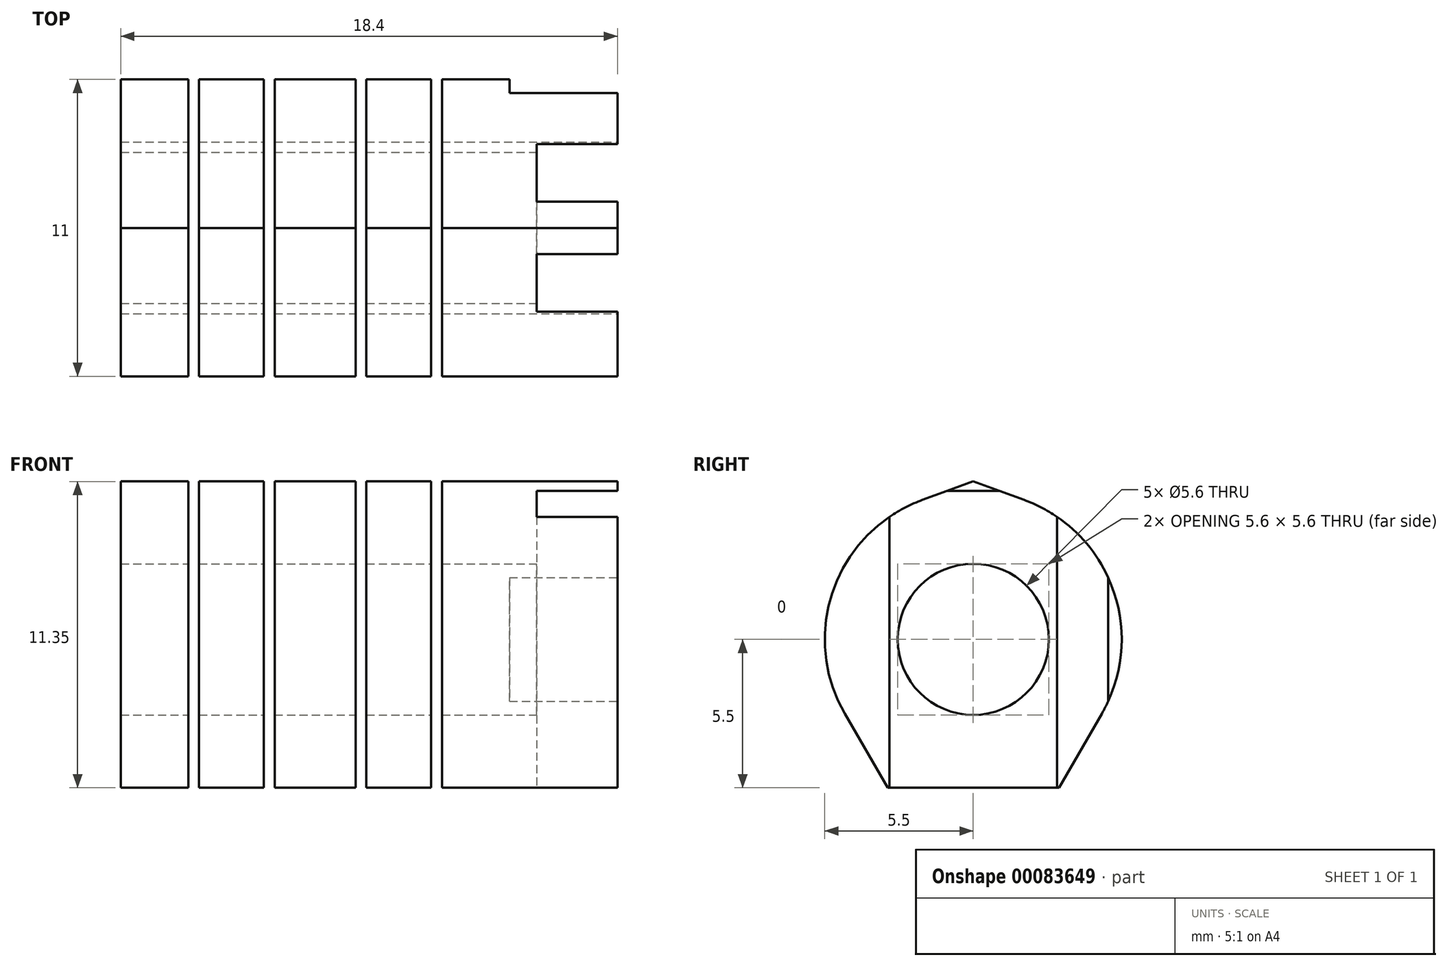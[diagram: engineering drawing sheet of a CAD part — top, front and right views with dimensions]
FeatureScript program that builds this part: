
annotation { "Feature Type Name" : "Feature", "Feature Type Description" : "" }
export const myFeature = defineFeature(function(context is Context, id is Id, definition is map)
    precondition{}
    {
        {
            var Q0;
            Q0=qCreatedBy(makeId("Top.planeOp"),FACE);
            var sketch = newSketch(context, id + "F0", { "sketchPlane" : qUnion([Q0])});
            skLineSegment(sketch, "E0", {"start": v(0, 0) * mm, "end": v(0, 9.5) * mm, "construction": true});
            skLineSegment(sketch, "E1", {"start": v(0, 5.5) * mm, "end": v(1.5, 5.5) * mm});
            skLineSegment(sketch, "E2", {"start": v(1.5, 5.5) * mm, "end": v(1.5, -8) * mm});
            skLineSegment(sketch, "E3", {"start": v(1.5, -8) * mm, "end": v(4.7, -8) * mm});
            skLineSegment(sketch, "E4", {"start": v(4.7, -8) * mm, "end": v(4.7, 5.5) * mm});
            skLineSegment(sketch, "E5", {"start": v(4.7, 5.5) * mm, "end": v(7.2, 5.5) * mm});
            skLineSegment(sketch, "E6", {"start": v(7.2, 5.5) * mm, "end": v(7.2, 5) * mm});
            skLineSegment(sketch, "E7", {"start": v(7.2, 5) * mm, "end": v(11.2, 5) * mm});
            skLineSegment(sketch, "E8", {"start": v(11.2, 5) * mm, "end": v(11.2, -9) * mm});
            skLineSegment(sketch, "E9", {"start": v(11.2, -9) * mm, "end": v(-7.2, -9) * mm});
            skLineSegment(sketch, "E10", {"start": v(-7.2, -9) * mm, "end": v(-7.2, 5.5) * mm});
            skLineSegment(sketch, "E11", {"start": v(-7.2, 5.5) * mm, "end": v(-4.7, 5.5) * mm});
            skLineSegment(sketch, "E12", {"start": v(-4.7, 5.5) * mm, "end": v(-4.7, -8) * mm});
            skLineSegment(sketch, "E13", {"start": v(-4.7, -8) * mm, "end": v(-1.5, -8) * mm});
            skLineSegment(sketch, "E14", {"start": v(-1.5, -8) * mm, "end": v(-1.5, 5.5) * mm});
            skLineSegment(sketch, "E15", {"start": v(-1.5, 5.5) * mm, "end": v(0, 5.5) * mm});
            skLineSegment(sketch, "E16", {"start": v(-4.7, 5.5) * mm, "end": v(-1.5, 5.5) * mm, "construction": true});
            skLineSegment(sketch, "E17", {"start": v(1.5, 5.5) * mm, "end": v(4.7, 5.5) * mm, "construction": true});
            skLineSegment(sketch, "E18", {"start": v(0, 9.5) * mm, "end": v(-7.3, 9.5) * mm});
            skLineSegment(sketch, "E19", {"start": v(-7.3, 9.5) * mm, "end": v(-7.3, 8.5) * mm});
            skLineSegment(sketch, "E20", {"start": v(-7.3, 8.5) * mm, "end": v(-4.3, 8.5) * mm});
            skLineSegment(sketch, "E21", {"start": v(-4.3, 8.5) * mm, "end": v(-4.3, -6.5) * mm});
            skLineSegment(sketch, "E22", {"start": v(-4.3, -6.5) * mm, "end": v(-1.9, -6.5) * mm});
            skLineSegment(sketch, "E23", {"start": v(-1.9, -6.5) * mm, "end": v(-1.9, 8.5) * mm});
            skPoint(sketch, "E23.endSnap0", {"position": v(-5.8, 8.5) * mm});
            skLineSegment(sketch, "E24", {"start": v(-1.9, 8.5) * mm, "end": v(0, 8.5) * mm});
            skLineSegment(sketch, "E25.MirrorCS", {"start": v(0, 9.5) * mm, "end": v(7.3, 9.5) * mm});
            skLineSegment(sketch, "E26.MirrorCS", {"start": v(7.3, 9.5) * mm, "end": v(7.3, 8.5) * mm});
            skLineSegment(sketch, "E27.MirrorCS", {"start": v(7.3, 8.5) * mm, "end": v(4.3, 8.5) * mm});
            skLineSegment(sketch, "E28.MirrorCS", {"start": v(4.3, 8.5) * mm, "end": v(4.3, -6.5) * mm});
            skLineSegment(sketch, "E29.MirrorCS", {"start": v(1.9, -6.5) * mm, "end": v(1.9, 8.5) * mm});
            skLineSegment(sketch, "E30.MirrorCS", {"start": v(1.9, 8.5) * mm, "end": v(0, 8.5) * mm});
            skLineSegment(sketch, "E31.MirrorCS", {"start": v(4.3, -6.5) * mm, "end": v(1.9, -6.5) * mm});
            skLineSegment(sketch, "E32", {"start": v(0, 0) * mm, "end": v(0, -9) * mm, "construction": true});
            skLineSegment(sketch, "E33", {"start": v(1.9, 8.5) * mm, "end": v(4.3, 8.5) * mm, "construction": true});
            skPoint(sketch, "E34", {"position": v(3.1, 8.5) * mm});
            skPoint(sketch, "E35", {"position": v(3.1, -8) * mm});
            skSolve(sketch);
        }
        {
            var Q0;
            Q0=makeQuery(id+"F0.imprint","IMPRINT",FACE,{"disambiguationData":[TD([[makeQuery(id+"F0.imprint","IMPRINT",EDGE,{"derivedFrom":sQuery(id+"F0.wireOp",EDGE,"E18")}),1.0]])]});
            var Q1;
            Q1=makeQuery(id+"F0.imprint","IMPRINT",FACE,{"disambiguationData":[TD([[makeQuery(id+"F0.imprint","IMPRINT",EDGE,{"derivedFrom":sQuery(id+"F0.wireOp",EDGE,"E1")}),-1.0]])]});
            extrude(context, id + "F1", {"entities" : qUnion([Q0, Q1]), "depth" : 25 * mm});
        }
        {
            var Q0;
            Q0=qCreatedBy(makeId("Right.planeOp"),FACE);
            var sketch = newSketch(context, id + "F2", { "sketchPlane" : qUnion([Q0])});
            skLineSegment(sketch, "E36", {"start": v(0, 0) * mm, "end": v(0, 5.5) * mm, "construction": true});
            skCircle(sketch, "E37", {"center": v(0, 5.5) * mm, "radius": 2.8 * mm});
            skCircle(sketch, "E38", {"center": v(0, 5.5) * mm, "radius": 5.5 * mm});
            skLineSegment(sketch, "E39", {"start": v(1.88, 10.67) * mm, "end": v(-37.5, 25) * mm});
            skLineSegment(sketch, "E40", {"start": v(-1.88, 10.67) * mm, "end": v(37.5, 25) * mm});
            skLineSegment(sketch, "E41", {"start": v(-37.5, 25) * mm, "end": v(37.5, 25) * mm});
            skLineSegment(sketch, "E42", {"start": v(-37.5, 25) * mm, "end": v(-37.5, 0) * mm});
            skLineSegment(sketch, "E43", {"start": v(-37.5, 0) * mm, "end": v(0, 0) * mm});
            skLineSegment(sketch, "E44", {"start": v(0, 0) * mm, "end": v(37.5, 0) * mm});
            skLineSegment(sketch, "E45", {"start": v(37.5, 0) * mm, "end": v(37.5, 25) * mm});
            skLineSegment(sketch, "E46", {"start": v(-4.76, 2.75) * mm, "end": v(-3.18, 0) * mm});
            skLineSegment(sketch, "E47", {"start": v(4.76, 2.75) * mm, "end": v(3.18, 0) * mm});
            skSolve(sketch);
        }
        {
            var Q0;
            Q0=makeQuery(id+"F2.imprint","IMPRINT",FACE,{"disambiguationData":[TD([[makeQuery(id+"F2.imprint","IMPRINT",EDGE,{"derivedFrom":sQuery(id+"F2.wireOp",EDGE,"E37")}),1.0]])]});
            extrude(context, id + "F3", {"entities" : qUnion([Q0]), "operationType" : NewBodyOperationType.REMOVE, "endBound" : BoundingType.THROUGH_ALL, "oppositeDirection" : true, "depth" : 25 * mm, "hasSecondDirection" : true, "secondDirectionBound" : SecondDirectionBoundingType.THROUGH_ALL, "secondDirectionOppositeDirection" : false, "secondDirectionDepth" : 25 * mm});
        }
        {
            var Q0;
            {var subQ0=sQuery(id+"F2.wireOp",EDGE,"E41");Q0=makeQuery(id+"F2.imprint","IMPRINT",FACE,{"disambiguationData":[TD([[makeQuery(id+"F2.imprint","IMPRINT",EDGE,{"derivedFrom":subQ0}),-1.0]])]});}
            var Q1;
            {var subQ0=sQuery(id+"F2.wireOp",EDGE,"E45");Q1=makeQuery(id+"F2.imprint","IMPRINT",FACE,{"disambiguationData":[TD([[makeQuery(id+"F2.imprint","IMPRINT",EDGE,{"derivedFrom":subQ0}),1.0]])]});}
            extrude(context, id + "F4", {"entities" : qUnion([Q0, Q1]), "operationType" : NewBodyOperationType.REMOVE, "endBound" : BoundingType.THROUGH_ALL, "oppositeDirection" : true, "depth" : 25 * mm, "hasSecondDirection" : true, "secondDirectionBound" : SecondDirectionBoundingType.THROUGH_ALL, "secondDirectionOppositeDirection" : false, "secondDirectionDepth" : 25 * mm});
        }
        {
            var Q0;
            {var subQ0=sQuery(id+"F2.wireOp",EDGE,"E41");Q0=makeQuery(id+"F2.imprint","IMPRINT",FACE,{"disambiguationData":[TD([[makeQuery(id+"F2.imprint","IMPRINT",EDGE,{"derivedFrom":subQ0}),-1.0]])]});}
            var Q1;
            {var subQ5=sQuery(id+"F2.wireOp",EDGE,"E42");Q1=makeQuery(id+"F2.imprint","IMPRINT",FACE,{"disambiguationData":[TD([[makeQuery(id+"F2.imprint","IMPRINT",EDGE,{"derivedFrom":subQ5}),1.0]])]});}
            extrude(context, id + "F5", {"entities" : qUnion([Q0, Q1]), "operationType" : NewBodyOperationType.REMOVE, "endBound" : BoundingType.THROUGH_ALL, "oppositeDirection" : true, "depth" : 25 * mm, "hasSecondDirection" : true, "secondDirectionBound" : SecondDirectionBoundingType.THROUGH_ALL, "secondDirectionOppositeDirection" : false, "secondDirectionDepth" : 25 * mm});
        }
        {
            var Q0;
            Q0=makeQuery(id+"F1.opExtrude","SWEPT_FACE",FACE,{"disambiguationData":[OSD([sQuery(id+"F0.wireOp",EDGE,"E8")])]});
            var sketch = newSketch(context, id + "F6", { "sketchPlane" : qUnion([Q0])});
            skCircle(sketch, "E48.0", {"center": v(0, 5.5) * mm, "radius": 2.8 * mm});
            skLineSegment(sketch, "E49.bottom", {"start": v(3.1, 11) * mm, "end": v(-3.1, 11) * mm});
            skLineSegment(sketch, "E49.top", {"start": v(3.1, 0) * mm, "end": v(-3.1, 0) * mm});
            skLineSegment(sketch, "E49.left", {"start": v(3.1, 11) * mm, "end": v(3.1, 0) * mm});
            skLineSegment(sketch, "E49.right", {"start": v(-3.1, 11) * mm, "end": v(-3.1, 0) * mm});
            skSolve(sketch);
        }
        {
            var Q0;
            Q0 = qSketchRegion(id + "F6", true);
            extrude(context, id + "F7", {"entities" : qUnion([Q0]), "operationType" : NewBodyOperationType.REMOVE, "oppositeDirection" : true, "depth" : 3 * mm});
        }
    });
